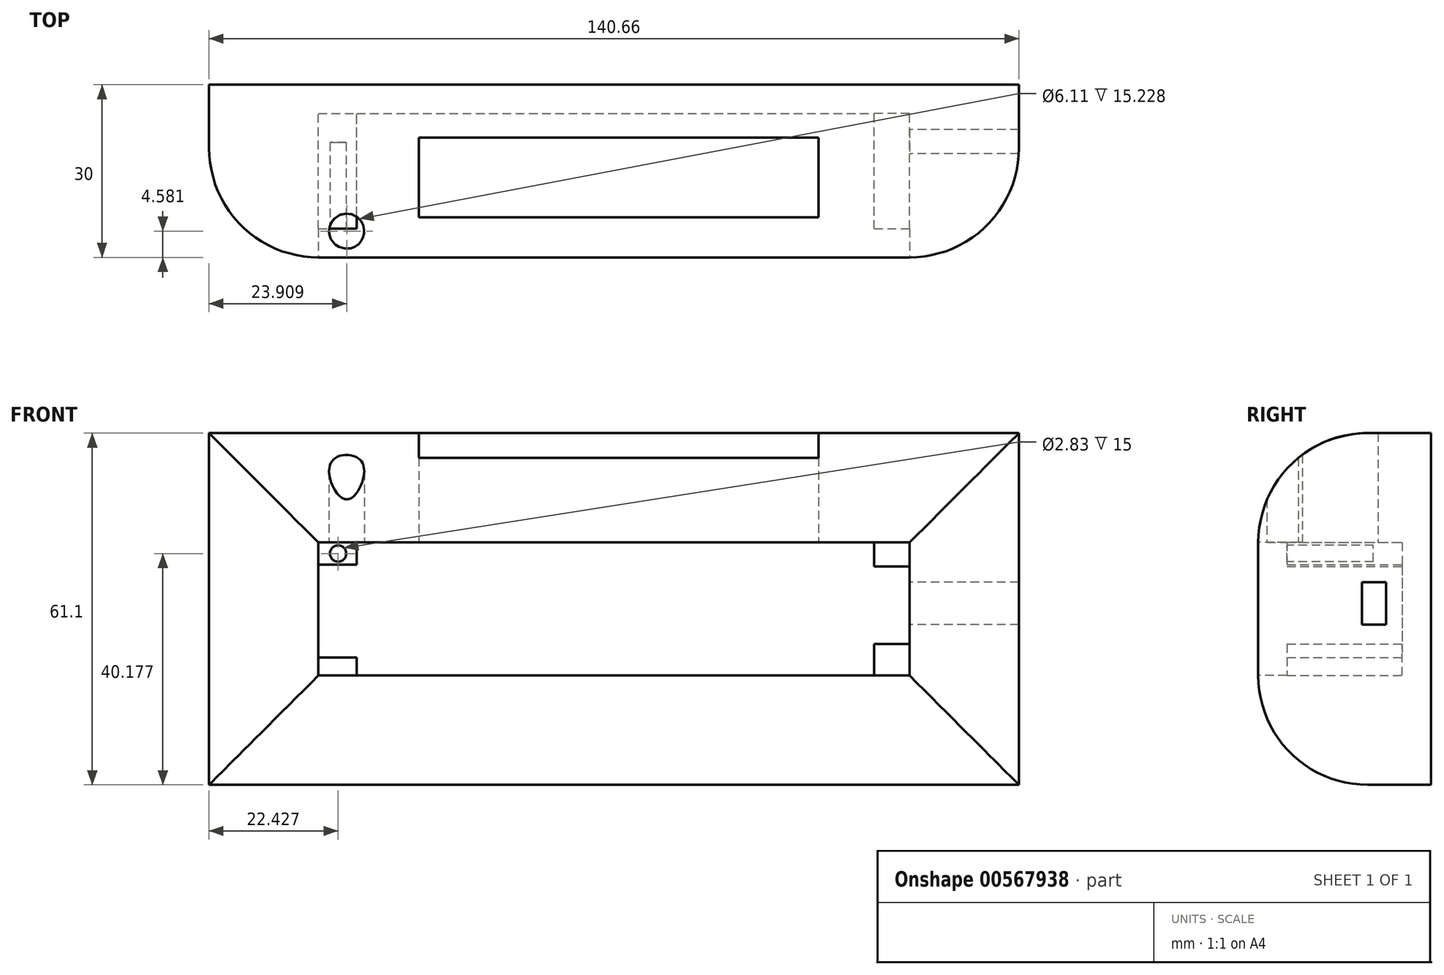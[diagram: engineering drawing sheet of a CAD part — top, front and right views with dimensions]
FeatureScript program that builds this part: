
annotation { "Feature Type Name" : "Feature", "Feature Type Description" : "" }
export const myFeature = defineFeature(function(context is Context, id is Id, definition is map)
    precondition{}
    {
        {
            var Q0;
            Q0=qCreatedBy(makeId("Front.planeOp"),FACE);
            var sketch = newSketch(context, id + "F0", { "sketchPlane" : qUnion([Q0])});
            skLineSegment(sketch, "E0.bottom", {"start": v(-70.33, 30.55) * mm, "end": v(70.33, 30.55) * mm});
            skLineSegment(sketch, "E0.top", {"start": v(-70.33, -30.55) * mm, "end": v(70.33, -30.55) * mm});
            skLineSegment(sketch, "E0.left", {"start": v(-70.33, 30.55) * mm, "end": v(-70.33, -30.55) * mm});
            skLineSegment(sketch, "E0.right", {"start": v(70.33, 30.55) * mm, "end": v(70.33, -30.55) * mm});
            skPoint(sketch, "E0.middle", {"position": v(0, 0) * mm});
            skSolve(sketch);
        }
        {
            var Q0;
            Q0 = qSketchRegion(id + "F0", true);
            extrude(context, id + "F1", {"entities" : qUnion([Q0]), "depth" : 30 * mm, "offsetDistance" : 25.4 * mm});
        }
        {
            var Q0;
            Q0=makeQuery(id+"F1.opExtrude","CAP_FACE",FACE,{"disambiguationData":[OSD([sQuery(id+"F0.wireOp",EDGE,"E0.bottom"),sQuery(id+"F0.wireOp",EDGE,"E0.top"),sQuery(id+"F0.wireOp",EDGE,"E0.left"),sQuery(id+"F0.wireOp",EDGE,"E0.right")])],"isStart":false});
            fillet(context, id + "F2", {"entities" : qUnion([Q0]), "radius" : 19 * mm, "tangentPropagation" : true, "allowEdgeOverflow" : false});
        }
        {
            var Q0;
            Q0=makeQuery(id+"F1.opExtrude","CAP_FACE",FACE,{"disambiguationData":[OSD([sQuery(id+"F0.wireOp",EDGE,"E0.bottom"),sQuery(id+"F0.wireOp",EDGE,"E0.top"),sQuery(id+"F0.wireOp",EDGE,"E0.left"),sQuery(id+"F0.wireOp",EDGE,"E0.right")])],"isStart":false});
            var sketch = newSketch(context, id + "F3", { "sketchPlane" : qUnion([Q0])});
            skSolve(sketch);
        }
        {
            var Q0;
            {var subQ0=sQuery(id+"F0.wireOp",EDGE,"E0.right");var subQ1=sQuery(id+"F0.wireOp",EDGE,"E0.left");var subQ2=sQuery(id+"F0.wireOp",EDGE,"E0.top");var subQ3=sQuery(id+"F0.wireOp",EDGE,"E0.bottom");var subQ4=makeQuery(id+"F1.opExtrude","CAP_FACE",FACE,{"disambiguationData":[OSD([subQ3,subQ2,subQ1,subQ0])],"isStart":false});Q0=makeQuery(id+"F3.imprint","IMPRINT",FACE,{"disambiguationData":[TD([[makeQuery(id+"F3.imprint","IMPRINT",EDGE,{"derivedFrom":makeQuery(id+"F2.opFillet","BLEND_EDGE",EDGE,{"blendedFrom":[makeQuery(id+"F1.opExtrude","CAP_EDGE",EDGE,{"disambiguationData":[OSD([subQ3])],"isStart":false}),subQ4],"blendedInto":[subQ4]})}),1.0]])]});}
            extrude(context, id + "F4", {"entities" : qUnion([Q0]), "operationType" : NewBodyOperationType.REMOVE, "oppositeDirection" : true, "depth" : 25 * mm, "offsetDistance" : 25 * mm});
        }
        {
            var Q0;
            {var subQ0=sQuery(id+"F0.wireOp",EDGE,"E0.right");var subQ1=sQuery(id+"F0.wireOp",EDGE,"E0.left");var subQ2=sQuery(id+"F0.wireOp",EDGE,"E0.top");var subQ3=sQuery(id+"F0.wireOp",EDGE,"E0.bottom");Q0=makeQuery(id+"F4.boolean.opBoolean","COPY",FACE,{"derivedFrom":makeQuery(id+"F4.opExtrude","SWEPT_FACE",FACE,{"disambiguationData":[OSD([subQ3,subQ2,subQ1,subQ0]),TDD([makeQuery(id+"F3.imprint","IMPRINT",EDGE,{"derivedFrom":makeQuery(id+"F2.opFillet","BLEND_EDGE",EDGE,{"blendedFrom":[makeQuery(id+"F1.opExtrude","CAP_EDGE",EDGE,{"disambiguationData":[OSD([subQ0])],"isStart":false}),makeQuery(id+"F1.opExtrude","CAP_FACE",FACE,{"disambiguationData":[OSD([subQ3,subQ2,subQ1,subQ0])],"isStart":false})],"blendedInto":[makeQuery(id+"F1.opExtrude","CAP_FACE",FACE,{"disambiguationData":[OSD([subQ3,subQ2,subQ1,subQ0])],"isStart":false})]})})])]})});}
            var sketch = newSketch(context, id + "F5", { "sketchPlane" : qUnion([Q0])});
            skLineSegment(sketch, "E1.bottom", {"start": v(7.77, 4.67) * mm, "end": v(11.97, 4.67) * mm});
            skLineSegment(sketch, "E1.top", {"start": v(7.77, -2.74) * mm, "end": v(11.97, -2.74) * mm});
            skLineSegment(sketch, "E1.left", {"start": v(7.77, 4.67) * mm, "end": v(7.77, -2.74) * mm});
            skLineSegment(sketch, "E1.right", {"start": v(11.97, 4.67) * mm, "end": v(11.97, -2.74) * mm});
            skSolve(sketch);
        }
        {
            var Q0;
            Q0 = qSketchRegion(id + "F5", true);
            extrude(context, id + "F6", {"entities" : qUnion([Q0]), "operationType" : NewBodyOperationType.REMOVE, "oppositeDirection" : true, "depth" : 55.3 * mm, "offsetDistance" : 25 * mm});
        }
        {
            var Q0;
            {var subQ0=sQuery(id+"F0.wireOp",EDGE,"E0.right");var subQ1=sQuery(id+"F0.wireOp",EDGE,"E0.left");var subQ2=sQuery(id+"F0.wireOp",EDGE,"E0.top");var subQ3=sQuery(id+"F0.wireOp",EDGE,"E0.bottom");Q0=makeQuery(id+"F4.boolean.opBoolean","COPY",FACE,{"derivedFrom":makeQuery(id+"F4.opExtrude","SWEPT_FACE",FACE,{"disambiguationData":[OSD([subQ3,subQ2,subQ1,subQ0]),TDD([makeQuery(id+"F3.imprint","IMPRINT",EDGE,{"derivedFrom":makeQuery(id+"F2.opFillet","BLEND_EDGE",EDGE,{"blendedFrom":[makeQuery(id+"F1.opExtrude","CAP_EDGE",EDGE,{"disambiguationData":[OSD([subQ3])],"isStart":false}),makeQuery(id+"F1.opExtrude","CAP_FACE",FACE,{"disambiguationData":[OSD([subQ3,subQ2,subQ1,subQ0])],"isStart":false})],"blendedInto":[makeQuery(id+"F1.opExtrude","CAP_FACE",FACE,{"disambiguationData":[OSD([subQ3,subQ2,subQ1,subQ0])],"isStart":false})]})})])]})});}
            var sketch = newSketch(context, id + "F7", { "sketchPlane" : qUnion([Q0])});
            skLineSegment(sketch, "E2.bottom", {"start": v(-33.85, 23.03) * mm, "end": v(35.54, 23.03) * mm});
            skLineSegment(sketch, "E2.top", {"start": v(-33.85, 9.19) * mm, "end": v(35.54, 9.19) * mm});
            skLineSegment(sketch, "E2.left", {"start": v(-33.85, 23.03) * mm, "end": v(-33.85, 9.19) * mm});
            skLineSegment(sketch, "E2.right", {"start": v(35.54, 23.03) * mm, "end": v(35.54, 9.19) * mm});
            skSolve(sketch);
        }
        {
            var Q0;
            Q0 = qSketchRegion(id + "F7", true);
            extrude(context, id + "F8", {"entities" : qUnion([Q0]), "operationType" : NewBodyOperationType.REMOVE, "oppositeDirection" : true, "depth" : 54.5 * mm, "offsetDistance" : 25 * mm});
        }
        {
            var Q0;
            {var subQ0=sQuery(id+"F0.wireOp",EDGE,"E0.right");var subQ1=sQuery(id+"F0.wireOp",EDGE,"E0.left");var subQ2=sQuery(id+"F0.wireOp",EDGE,"E0.top");var subQ3=sQuery(id+"F0.wireOp",EDGE,"E0.bottom");Q0=makeQuery(id+"F4.boolean.opBoolean","COPY",FACE,{"derivedFrom":makeQuery(id+"F4.opExtrude","SWEPT_FACE",FACE,{"disambiguationData":[OSD([subQ3,subQ2,subQ1,subQ0]),TDD([makeQuery(id+"F3.imprint","IMPRINT",EDGE,{"derivedFrom":makeQuery(id+"F2.opFillet","BLEND_EDGE",EDGE,{"blendedFrom":[makeQuery(id+"F1.opExtrude","CAP_EDGE",EDGE,{"disambiguationData":[OSD([subQ3])],"isStart":false}),makeQuery(id+"F1.opExtrude","CAP_FACE",FACE,{"disambiguationData":[OSD([subQ3,subQ2,subQ1,subQ0])],"isStart":false})],"blendedInto":[makeQuery(id+"F1.opExtrude","CAP_FACE",FACE,{"disambiguationData":[OSD([subQ3,subQ2,subQ1,subQ0])],"isStart":false})]})})])]})});}
            var sketch = newSketch(context, id + "F9", { "sketchPlane" : qUnion([Q0])});
            skCircle(sketch, "E3", {"center": v(-46.42, 25.42) * mm, "radius": 3.06 * mm});
            skSolve(sketch);
        }
        {
            var Q0;
            Q0 = qSketchRegion(id + "F9", true);
            extrude(context, id + "F10", {"entities" : qUnion([Q0]), "operationType" : NewBodyOperationType.REMOVE, "oppositeDirection" : true, "depth" : 61.9 * mm, "offsetDistance" : 25 * mm});
        }
        {
            var Q0;
            Q0=makeQuery(id+"F4.boolean.opBoolean","COPY",FACE,{"derivedFrom":makeQuery(id+"F4.opExtrude","CAP_FACE",FACE,{"disambiguationData":[OSD([sQuery(id+"F0.wireOp",EDGE,"E0.bottom"),sQuery(id+"F0.wireOp",EDGE,"E0.top"),sQuery(id+"F0.wireOp",EDGE,"E0.left"),sQuery(id+"F0.wireOp",EDGE,"E0.right")])],"isStart":false})});
            var sketch = newSketch(context, id + "F11", { "sketchPlane" : qUnion([Q0])});
            skLineSegment(sketch, "E4.bottom", {"start": v(-51.33, -11.55) * mm, "end": v(-44.67, -11.55) * mm});
            skLineSegment(sketch, "E4.top", {"start": v(-51.33, -8.44) * mm, "end": v(-44.67, -8.44) * mm});
            skLineSegment(sketch, "E4.left", {"start": v(-51.33, -11.55) * mm, "end": v(-51.33, -8.44) * mm});
            skLineSegment(sketch, "E4.right", {"start": v(-44.67, -11.55) * mm, "end": v(-44.67, -8.44) * mm});
            skLineSegment(sketch, "E5.bottom", {"start": v(-51.33, 11.55) * mm, "end": v(-44.67, 11.55) * mm});
            skLineSegment(sketch, "E5.top", {"start": v(-51.33, 7.7) * mm, "end": v(-44.67, 7.7) * mm});
            skLineSegment(sketch, "E5.left", {"start": v(-51.33, 11.55) * mm, "end": v(-51.33, 7.7) * mm});
            skLineSegment(sketch, "E5.right", {"start": v(-44.67, 11.55) * mm, "end": v(-44.67, 7.7) * mm});
            skLineSegment(sketch, "E6.bottom", {"start": v(51.33, 11.55) * mm, "end": v(45.2, 11.55) * mm});
            skLineSegment(sketch, "E6.top", {"start": v(51.33, 7.36) * mm, "end": v(45.2, 7.36) * mm});
            skLineSegment(sketch, "E6.left", {"start": v(51.33, 11.55) * mm, "end": v(51.33, 7.36) * mm});
            skLineSegment(sketch, "E6.right", {"start": v(45.2, 11.55) * mm, "end": v(45.2, 7.36) * mm});
            skLineSegment(sketch, "E7.bottom", {"start": v(51.33, -11.55) * mm, "end": v(45.2, -11.55) * mm});
            skLineSegment(sketch, "E7.top", {"start": v(51.33, -6.1) * mm, "end": v(45.2, -6.1) * mm});
            skLineSegment(sketch, "E7.left", {"start": v(51.33, -11.55) * mm, "end": v(51.33, -6.1) * mm});
            skLineSegment(sketch, "E7.right", {"start": v(45.2, -11.55) * mm, "end": v(45.2, -6.1) * mm});
            skSolve(sketch);
        }
        {
            var Q0;
            Q0 = qSketchRegion(id + "F11", true);
            extrude(context, id + "F12", {"entities" : qUnion([Q0]), "operationType" : NewBodyOperationType.ADD, "depth" : 20 * mm, "offsetDistance" : 25 * mm});
        }
        {
            var Q0;
            Q0=makeQuery(id+"F12.opExtrude","CAP_FACE",FACE,{"disambiguationData":[OSD([sQuery(id+"F11.wireOp",EDGE,"E5.bottom"),sQuery(id+"F11.wireOp",EDGE,"E5.top"),sQuery(id+"F11.wireOp",EDGE,"E5.left"),sQuery(id+"F11.wireOp",EDGE,"E5.right")])],"isStart":false});
            var sketch = newSketch(context, id + "F13", { "sketchPlane" : qUnion([Q0])});
            skCircle(sketch, "E8", {"center": v(-47.9, 9.63) * mm, "radius": 1.42 * mm});
            skPoint(sketch, "E8.centerSnap0", {"position": v(-44.67, 9.63) * mm});
            skSolve(sketch);
        }
        {
            var Q0;
            Q0 = qSketchRegion(id + "F13", true);
            extrude(context, id + "F14", {"entities" : qUnion([Q0]), "operationType" : NewBodyOperationType.REMOVE, "oppositeDirection" : true, "depth" : 15 * mm, "offsetDistance" : 25 * mm});
        }
    });
